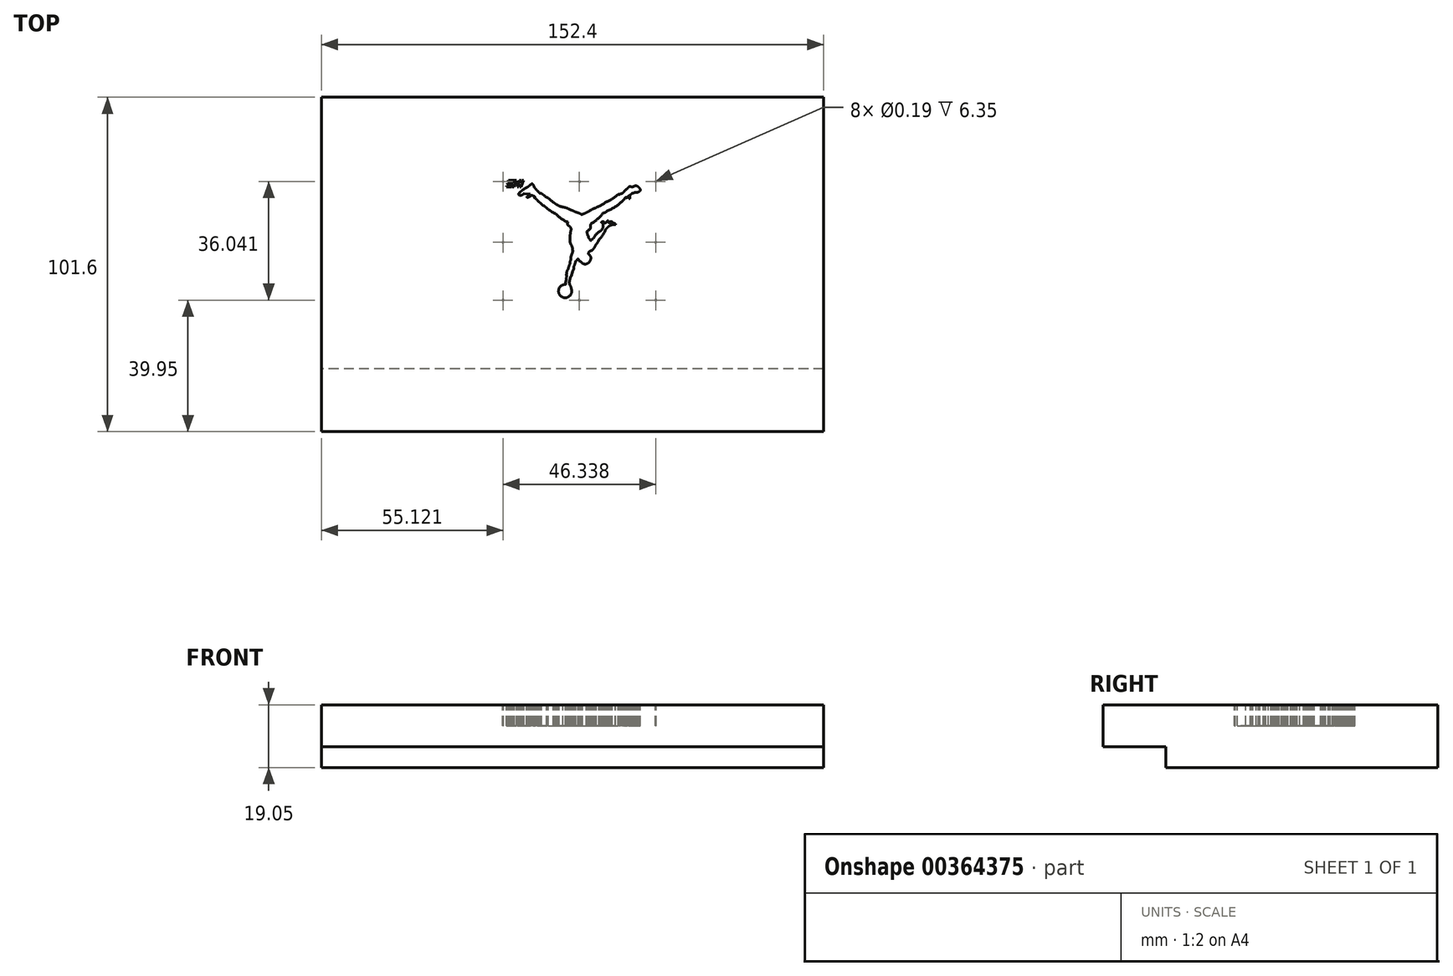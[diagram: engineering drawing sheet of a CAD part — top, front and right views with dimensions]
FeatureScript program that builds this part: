
annotation { "Feature Type Name" : "Feature", "Feature Type Description" : "" }
export const myFeature = defineFeature(function(context is Context, id is Id, definition is map)
    precondition{}
    {
        {
            var Q0;
            Q0=qCreatedBy(makeId("Top.planeOp"),FACE);
            var sketch = newSketch(context, id + "F0", { "sketchPlane" : qUnion([Q0])});
            skLineSegment(sketch, "E0.bottom", {"start": v(-78.3, 43.63) * mm, "end": v(74.1, 43.63) * mm});
            skLineSegment(sketch, "E0.top", {"start": v(-78.3, -57.97) * mm, "end": v(74.1, -57.97) * mm});
            skLineSegment(sketch, "E0.left", {"start": v(-78.3, 43.63) * mm, "end": v(-78.3, -57.97) * mm});
            skLineSegment(sketch, "E0.right", {"start": v(74.1, 43.63) * mm, "end": v(74.1, -57.97) * mm});
            skSolve(sketch);
        }
        {
            var Q0;
            Q0 = qSketchRegion(id + "F0", true);
            extrude(context, id + "F1", {"entities" : qUnion([Q0]), "depth" : 19.05 * mm});
        }
        {
            var Q0;
            Q0=makeQuery(id+"F1.opExtrude","CAP_FACE",FACE,{"disambiguationData":[OSD([sQuery(id+"F0.wireOp",EDGE,"E0.bottom"),sQuery(id+"F0.wireOp",EDGE,"E0.top"),sQuery(id+"F0.wireOp",EDGE,"E0.left"),sQuery(id+"F0.wireOp",EDGE,"E0.right")])],"isStart":true});
            var sketch = newSketch(context, id + "F2", { "sketchPlane" : qUnion([Q0])});
            skLineSegment(sketch, "E1.bottom", {"start": v(74.1, 57.97) * mm, "end": v(-78.3, 57.97) * mm});
            skLineSegment(sketch, "E1.top", {"start": v(74.1, 38.92) * mm, "end": v(-78.3, 38.92) * mm});
            skLineSegment(sketch, "E1.left", {"start": v(74.1, 57.97) * mm, "end": v(74.1, 38.92) * mm});
            skLineSegment(sketch, "E1.right", {"start": v(-78.3, 57.97) * mm, "end": v(-78.3, 38.92) * mm});
            skSolve(sketch);
        }
        {
            var Q0;
            Q0 = qSketchRegion(id + "F2", true);
            extrude(context, id + "F3", {"entities" : qUnion([Q0]), "operationType" : NewBodyOperationType.REMOVE, "oppositeDirection" : true, "depth" : 6.35 * mm});
        }
        {
            var Q0;
            Q0=makeQuery(id+"F1.opExtrude","CAP_FACE",FACE,{"disambiguationData":[OSD([sQuery(id+"F0.wireOp",EDGE,"E0.bottom"),sQuery(id+"F0.wireOp",EDGE,"E0.top"),sQuery(id+"F0.wireOp",EDGE,"E0.left"),sQuery(id+"F0.wireOp",EDGE,"E0.right")])],"isStart":false});
            var sketch = newSketch(context, id + "F4", { "sketchPlane" : qUnion([Q0])});
            skLineSegment(sketch, "E2", {"start": v(-20.56, 18.4) * mm, "end": v(-21.26, 16.34) * mm});
            skLineSegment(sketch, "E3", {"start": v(-21.26, 16.34) * mm, "end": v(-22.15, 16.34) * mm});
            skLineSegment(sketch, "E4", {"start": v(-22.15, 16.34) * mm, "end": v(-22.01, 16.76) * mm});
            skLineSegment(sketch, "E5", {"start": v(-21.49, 18.4) * mm, "end": v(-20.56, 18.4) * mm});
            skLineSegment(sketch, "E6", {"start": v(-18.45, 16.34) * mm, "end": v(-18.9, 16.34) * mm});
            skLineSegment(sketch, "E7", {"start": v(-18.9, 16.34) * mm, "end": v(-18.2, 18.4) * mm});
            skLineSegment(sketch, "E8", {"start": v(-18.2, 18.4) * mm, "end": v(-17.73, 18.4) * mm});
            skLineSegment(sketch, "E9", {"start": v(-17.73, 18.4) * mm, "end": v(-17.77, 17.47) * mm});
            skLineSegment(sketch, "E10", {"start": v(-17.77, 17.47) * mm, "end": v(-17.45, 18.4) * mm});
            skLineSegment(sketch, "E11", {"start": v(-17.45, 18.4) * mm, "end": v(-17, 18.4) * mm});
            skLineSegment(sketch, "E12", {"start": v(-17, 18.4) * mm, "end": v(-17.7, 16.34) * mm});
            skLineSegment(sketch, "E13", {"start": v(-17.7, 16.34) * mm, "end": v(-18.15, 16.34) * mm});
            skLineSegment(sketch, "E14", {"start": v(-18.15, 16.34) * mm, "end": v(-18.14, 17.27) * mm});
            skLineSegment(sketch, "E15", {"start": v(-18.14, 17.27) * mm, "end": v(-18.45, 16.34) * mm});
            skLineSegment(sketch, "E16", {"start": v(-19.11, 16.34) * mm, "end": v(-19.65, 16.34) * mm});
            skLineSegment(sketch, "E17", {"start": v(-19.65, 16.34) * mm, "end": v(-18.95, 18.4) * mm});
            skLineSegment(sketch, "E18", {"start": v(-18.95, 18.4) * mm, "end": v(-18.41, 18.4) * mm});
            skLineSegment(sketch, "E19", {"start": v(-18.41, 18.4) * mm, "end": v(-19.11, 16.34) * mm, "construction": true});
            skLineSegment(sketch, "E20", {"start": v(-20.64, 16.34) * mm, "end": v(-21.14, 16.34) * mm});
            skLineSegment(sketch, "E21", {"start": v(-21.14, 16.34) * mm, "end": v(-20.52, 17.27) * mm});
            skLineSegment(sketch, "E22", {"start": v(-20.52, 17.27) * mm, "end": v(-20.47, 18.4) * mm});
            skLineSegment(sketch, "E23", {"start": v(-20.47, 18.4) * mm, "end": v(-19.92, 18.4) * mm});
            skLineSegment(sketch, "E24", {"start": v(-19.92, 18.4) * mm, "end": v(-20, 17.52) * mm});
            skLineSegment(sketch, "E25", {"start": v(-20, 17.52) * mm, "end": v(-19.7, 18.4) * mm});
            skLineSegment(sketch, "E26", {"start": v(-19.7, 18.4) * mm, "end": v(-19.16, 18.4) * mm});
            skLineSegment(sketch, "E27", {"start": v(-19.16, 18.4) * mm, "end": v(-19.86, 16.34) * mm});
            skLineSegment(sketch, "E28", {"start": v(-19.86, 16.34) * mm, "end": v(-20.4, 16.34) * mm});
            skLineSegment(sketch, "E29", {"start": v(-20.4, 16.34) * mm, "end": v(-20.12, 17.14) * mm});
            skLineSegment(sketch, "E30", {"start": v(-20.12, 17.14) * mm, "end": v(-20.64, 16.34) * mm});
            skCircle(sketch, "E31", {"center": v(23.17, 18.02) * mm, "radius": 0.1 * mm});
            skCircle(sketch, "E32", {"center": v(-23.17, 18.02) * mm, "radius": 0.1 * mm});
            skCircle(sketch, "E33", {"center": v(-23.17, -18.02) * mm, "radius": 0.1 * mm});
            skCircle(sketch, "E34", {"center": v(23.17, -18.02) * mm, "radius": 0.1 * mm});
            skCircle(sketch, "E35", {"center": v(23.17, -0.48) * mm, "radius": 0.1 * mm});
            skCircle(sketch, "E36", {"center": v(0, 18.02) * mm, "radius": 0.1 * mm});
            skCircle(sketch, "E37", {"center": v(-23.17, -0.48) * mm, "radius": 0.1 * mm});
            skCircle(sketch, "E38", {"center": v(0, -18.02) * mm, "radius": 0.1 * mm});
            skLineSegment(sketch, "E39", {"start": v(-3.9, -10.55) * mm, "end": v(-4, -11.58) * mm});
            skLineSegment(sketch, "E40", {"start": v(24.2, 19.05) * mm, "end": v(-24.2, 19.05) * mm, "construction": true});
            skLineSegment(sketch, "E41", {"start": v(-24.2, -19.05) * mm, "end": v(24.2, -19.05) * mm, "construction": true});
            skLineSegment(sketch, "E42", {"start": v(24.2, -19.05) * mm, "end": v(24.2, 19.05) * mm, "construction": true});
            skLineSegment(sketch, "E43", {"start": v(-24.2, 19.05) * mm, "end": v(-24.2, -19.05) * mm, "construction": true});
            skArc(sketch, "E44", {"start": v(-3.94, -10.35) * mm, "mid": v(-3.93, -10.45) * mm, "end": v(-3.9, -10.55) * mm});
            skArc(sketch, "E45", {"start": v(-1.72, -7.9) * mm, "mid": v(-1.37, -7.08) * mm, "end": v(-1.13, -6.21) * mm});
            skArc(sketch, "E46", {"start": v(-1.13, -6.21) * mm, "mid": v(-1.1, -6.16) * mm, "end": v(-1.08, -6.1) * mm});
            skArc(sketch, "E47", {"start": v(-1.75, -8.61) * mm, "mid": v(-1.7, -8.26) * mm, "end": v(-1.72, -7.9) * mm});
            skArc(sketch, "E48", {"start": v(-2.12, -9.3) * mm, "mid": v(-1.92, -8.97) * mm, "end": v(-1.75, -8.61) * mm});
            skArc(sketch, "E49", {"start": v(-2.08, -9.41) * mm, "mid": v(-2.08, -9.35) * mm, "end": v(-2.12, -9.3) * mm});
            skLineSegment(sketch, "E50", {"start": v(-2.49, -10.76) * mm, "end": v(-2.08, -9.41) * mm});
            skArc(sketch, "E51", {"start": v(-2.68, -10.92) * mm, "mid": v(-2.56, -10.87) * mm, "end": v(-2.49, -10.76) * mm});
            skLineSegment(sketch, "E52", {"start": v(-3.12, -12.7) * mm, "end": v(-2.68, -10.92) * mm});
            skArc(sketch, "E53", {"start": v(-2.97, -13.33) * mm, "mid": v(-3.02, -13) * mm, "end": v(-3.12, -12.7) * mm});
            skArc(sketch, "E54", {"start": v(-2.44, -14.7) * mm, "mid": v(-2.62, -13.99) * mm, "end": v(-2.97, -13.33) * mm});
            skArc(sketch, "E55", {"start": v(-4.28, -13.3) * mm, "mid": v(-5.57, -16.9) * mm, "end": v(-2.44, -14.7) * mm});
            skArc(sketch, "E56", {"start": v(-4.28, -13.3) * mm, "mid": v(-4.13, -13.17) * mm, "end": v(-4.19, -12.98) * mm});
            skArc(sketch, "E57", {"start": v(-4.17, -12.53) * mm, "mid": v(-4.23, -12.76) * mm, "end": v(-4.19, -12.98) * mm});
            skArc(sketch, "E58", {"start": v(-4.17, -12.53) * mm, "mid": v(-4.06, -12.06) * mm, "end": v(-4, -11.58) * mm});
            skArc(sketch, "E59", {"start": v(-3.8, -9.3) * mm, "mid": v(-3.9, -9.82) * mm, "end": v(-3.94, -10.35) * mm});
            skArc(sketch, "E60", {"start": v(-3.44, -8.7) * mm, "mid": v(-3.68, -8.97) * mm, "end": v(-3.8, -9.3) * mm});
            skArc(sketch, "E61", {"start": v(-2.87, -6.92) * mm, "mid": v(-3.21, -7.8) * mm, "end": v(-3.44, -8.7) * mm});
            skArc(sketch, "E62", {"start": v(-2.66, -5.86) * mm, "mid": v(-2.83, -6.38) * mm, "end": v(-2.87, -6.92) * mm});
            skArc(sketch, "E63", {"start": v(-2.65, -5.2) * mm, "mid": v(-2.66, -5.53) * mm, "end": v(-2.66, -5.86) * mm});
            skArc(sketch, "E64", {"start": v(-2.47, -4.51) * mm, "mid": v(-2.59, -4.85) * mm, "end": v(-2.65, -5.2) * mm});
            skArc(sketch, "E65", {"start": v(-2.1, -3.69) * mm, "mid": v(-2.3, -4.1) * mm, "end": v(-2.47, -4.51) * mm});
            skArc(sketch, "E66", {"start": v(-2.1, -3.69) * mm, "mid": v(-2.06, -3.55) * mm, "end": v(-2.04, -3.4) * mm});
            skArc(sketch, "E67", {"start": v(-2.04, -3.4) * mm, "mid": v(-2.03, -3.08) * mm, "end": v(-2.04, -2.76) * mm});
            skArc(sketch, "E68", {"start": v(-2.04, -2.76) * mm, "mid": v(-2.11, -2.3) * mm, "end": v(-2.23, -1.83) * mm});
            skArc(sketch, "E69", {"start": v(-2.23, -1.83) * mm, "mid": v(-2.36, -1.49) * mm, "end": v(-2.54, -1.17) * mm});
            skArc(sketch, "E70", {"start": v(-2.8, -0.48) * mm, "mid": v(-2.71, -0.84) * mm, "end": v(-2.54, -1.17) * mm});
            skArc(sketch, "E71", {"start": v(-2.87, 0.87) * mm, "mid": v(-2.85, 0.2) * mm, "end": v(-2.8, -0.48) * mm});
            skArc(sketch, "E72", {"start": v(-2.48, 3.52) * mm, "mid": v(-2.76, 2.21) * mm, "end": v(-2.87, 0.87) * mm});
            skArc(sketch, "E73", {"start": v(-2.77, 4.24) * mm, "mid": v(-2.65, 3.87) * mm, "end": v(-2.48, 3.52) * mm});
            skArc(sketch, "E74", {"start": v(-3.56, 4.85) * mm, "mid": v(-3.2, 4.5) * mm, "end": v(-2.77, 4.24) * mm});
            skArc(sketch, "E75", {"start": v(-3.64, 5.38) * mm, "mid": v(-3.66, 5.1) * mm, "end": v(-3.56, 4.85) * mm});
            skArc(sketch, "E76", {"start": v(-3.5, 5.63) * mm, "mid": v(-3.57, 5.5) * mm, "end": v(-3.64, 5.38) * mm});
            skArc(sketch, "E77", {"start": v(-7.2, 8.26) * mm, "mid": v(-5.5, 6.72) * mm, "end": v(-3.5, 5.63) * mm});
            skArc(sketch, "E78", {"start": v(-7.96, 8.54) * mm, "mid": v(-7.6, 8.35) * mm, "end": v(-7.2, 8.26) * mm});
            skArc(sketch, "E79", {"start": v(-12.78, 12.33) * mm, "mid": v(-10.45, 10.33) * mm, "end": v(-7.96, 8.54) * mm});
            skArc(sketch, "E80", {"start": v(-12.78, 12.33) * mm, "mid": v(-13.08, 12.64) * mm, "end": v(-13.43, 12.89) * mm});
            skArc(sketch, "E81", {"start": v(-13.54, 12.94) * mm, "mid": v(-13.49, 12.91) * mm, "end": v(-13.43, 12.89) * mm});
            skArc(sketch, "E82", {"start": v(-13.6, 13.18) * mm, "mid": v(-13.63, 13.05) * mm, "end": v(-13.54, 12.94) * mm});
            skArc(sketch, "E83", {"start": v(-13.52, 13.33) * mm, "mid": v(-13.56, 13.25) * mm, "end": v(-13.6, 13.18) * mm});
            skArc(sketch, "E84", {"start": v(-13.52, 13.33) * mm, "mid": v(-13.6, 13.47) * mm, "end": v(-13.74, 13.54) * mm});
            skArc(sketch, "E85", {"start": v(-14.02, 13.56) * mm, "mid": v(-13.88, 13.53) * mm, "end": v(-13.74, 13.54) * mm});
            skArc(sketch, "E86", {"start": v(-14.02, 13.56) * mm, "mid": v(-14.15, 13.67) * mm, "end": v(-14.3, 13.78) * mm});
            skArc(sketch, "E87", {"start": v(-14.3, 13.78) * mm, "mid": v(-14.45, 13.82) * mm, "end": v(-14.6, 13.77) * mm});
            skArc(sketch, "E88", {"start": v(-14.6, 13.77) * mm, "mid": v(-14.7, 13.7) * mm, "end": v(-14.78, 13.6) * mm});
            skArc(sketch, "E89", {"start": v(-14.98, 13.6) * mm, "mid": v(-14.88, 13.59) * mm, "end": v(-14.78, 13.6) * mm});
            skArc(sketch, "E90", {"start": v(-15.76, 13.19) * mm, "mid": v(-15.32, 13.3) * mm, "end": v(-14.98, 13.6) * mm});
            skArc(sketch, "E91", {"start": v(-15.9, 13.18) * mm, "mid": v(-15.83, 13.18) * mm, "end": v(-15.76, 13.19) * mm});
            skArc(sketch, "E92", {"start": v(-15.93, 13.35) * mm, "mid": v(-15.98, 13.25) * mm, "end": v(-15.9, 13.18) * mm});
            skArc(sketch, "E93", {"start": v(-15.93, 13.35) * mm, "mid": v(-15.77, 13.39) * mm, "end": v(-15.62, 13.46) * mm});
            skArc(sketch, "E94", {"start": v(-15.62, 13.46) * mm, "mid": v(-15.21, 13.8) * mm, "end": v(-14.9, 14.23) * mm});
            skLineSegment(sketch, "E95", {"start": v(-16.8, 14.28) * mm, "end": v(-14.9, 14.23) * mm});
            skArc(sketch, "E96", {"start": v(-16.8, 14.28) * mm, "mid": v(-16.96, 14.22) * mm, "end": v(-17.1, 14.13) * mm});
            skArc(sketch, "E97", {"start": v(-17.67, 13.8) * mm, "mid": v(-17.37, 13.94) * mm, "end": v(-17.1, 14.13) * mm});
            skArc(sketch, "E98", {"start": v(-18.09, 13.8) * mm, "mid": v(-17.88, 13.77) * mm, "end": v(-17.67, 13.8) * mm});
            skArc(sketch, "E99", {"start": v(-18.46, 14.04) * mm, "mid": v(-18.3, 13.88) * mm, "end": v(-18.09, 13.8) * mm});
            skArc(sketch, "E100", {"start": v(-18.48, 14.26) * mm, "mid": v(-18.5, 14.15) * mm, "end": v(-18.46, 14.04) * mm});
            skArc(sketch, "E101", {"start": v(-17.16, 15.47) * mm, "mid": v(-17.84, 14.9) * mm, "end": v(-18.48, 14.26) * mm});
            skArc(sketch, "E102", {"start": v(-16.05, 16.16) * mm, "mid": v(-16.63, 15.85) * mm, "end": v(-17.16, 15.47) * mm});
            skArc(sketch, "E103", {"start": v(-16.05, 16.16) * mm, "mid": v(-15.58, 16.42) * mm, "end": v(-15.16, 16.75) * mm});
            skArc(sketch, "E104", {"start": v(-14.47, 17.28) * mm, "mid": v(-14.84, 17.05) * mm, "end": v(-15.16, 16.75) * mm});
            skArc(sketch, "E105", {"start": v(-14.19, 17.24) * mm, "mid": v(-14.32, 17.3) * mm, "end": v(-14.47, 17.28) * mm});
            skArc(sketch, "E106", {"start": v(-13.74, 16.38) * mm, "mid": v(-13.93, 16.83) * mm, "end": v(-14.19, 17.24) * mm});
            skArc(sketch, "E107", {"start": v(-13.72, 16.24) * mm, "mid": v(-13.73, 16.31) * mm, "end": v(-13.74, 16.38) * mm});
            skArc(sketch, "E108", {"start": v(-13.05, 15.43) * mm, "mid": v(-13.34, 15.87) * mm, "end": v(-13.72, 16.24) * mm});
            skArc(sketch, "E109", {"start": v(-12.41, 14.78) * mm, "mid": v(-12.7, 15.14) * mm, "end": v(-13.05, 15.43) * mm});
            skArc(sketch, "E110", {"start": v(-12.41, 14.78) * mm, "mid": v(-12.23, 14.6) * mm, "end": v(-12.03, 14.44) * mm});
            skArc(sketch, "E111", {"start": v(-11.5, 14.35) * mm, "mid": v(-11.76, 14.43) * mm, "end": v(-12.03, 14.44) * mm});
            skArc(sketch, "E112", {"start": v(-10.03, 13.2) * mm, "mid": v(-10.75, 13.8) * mm, "end": v(-11.5, 14.35) * mm});
            skArc(sketch, "E113", {"start": v(-9.42, 12.95) * mm, "mid": v(-9.71, 13.1) * mm, "end": v(-10.03, 13.2) * mm});
            skArc(sketch, "E114", {"start": v(-9.42, 12.95) * mm, "mid": v(-8.57, 12.2) * mm, "end": v(-7.66, 11.52) * mm});
            skArc(sketch, "E115", {"start": v(-7.66, 11.52) * mm, "mid": v(-7.3, 11.23) * mm, "end": v(-6.91, 10.98) * mm});
            skArc(sketch, "E116", {"start": v(-6.18, 10.54) * mm, "mid": v(-6.53, 10.79) * mm, "end": v(-6.91, 10.98) * mm});
            skArc(sketch, "E117", {"start": v(-6.18, 10.54) * mm, "mid": v(-5.6, 10.38) * mm, "end": v(-5.02, 10.25) * mm});
            skArc(sketch, "E118", {"start": v(-3.08, 9.6) * mm, "mid": v(-4.03, 10) * mm, "end": v(-5.02, 10.25) * mm});
            skArc(sketch, "E119", {"start": v(-3.08, 9.6) * mm, "mid": v(-2.81, 9.45) * mm, "end": v(-2.52, 9.33) * mm});
            skArc(sketch, "E120", {"start": v(-1.2, 8.76) * mm, "mid": v(-1.86, 9.06) * mm, "end": v(-2.52, 9.33) * mm});
            skArc(sketch, "E121", {"start": v(0.56, 8.04) * mm, "mid": v(-0.3, 8.45) * mm, "end": v(-1.2, 8.76) * mm});
            skArc(sketch, "E122", {"start": v(0.56, 8.04) * mm, "mid": v(0.77, 8) * mm, "end": v(0.98, 8.06) * mm});
            skArc(sketch, "E123", {"start": v(0.98, 8.06) * mm, "mid": v(1.95, 8.49) * mm, "end": v(2.89, 9) * mm});
            skArc(sketch, "E124", {"start": v(6.07, 10.48) * mm, "mid": v(4.44, 9.8) * mm, "end": v(2.89, 9) * mm});
            skArc(sketch, "E125", {"start": v(9.63, 12.55) * mm, "mid": v(7.81, 11.58) * mm, "end": v(6.07, 10.48) * mm});
            skArc(sketch, "E126", {"start": v(9.63, 12.55) * mm, "mid": v(10.73, 13.26) * mm, "end": v(11.76, 14.08) * mm});
            skArc(sketch, "E127", {"start": v(11.97, 14.1) * mm, "mid": v(11.86, 14.12) * mm, "end": v(11.76, 14.08) * mm});
            skArc(sketch, "E128", {"start": v(12.08, 14.05) * mm, "mid": v(12.03, 14.08) * mm, "end": v(11.97, 14.1) * mm});
            skArc(sketch, "E129", {"start": v(12.08, 14.05) * mm, "mid": v(12.15, 14.03) * mm, "end": v(12.2, 14.06) * mm});
            skArc(sketch, "E130", {"start": v(12.59, 14.33) * mm, "mid": v(12.4, 14.2) * mm, "end": v(12.2, 14.06) * mm});
            skArc(sketch, "E131", {"start": v(12.84, 14.36) * mm, "mid": v(12.71, 14.36) * mm, "end": v(12.59, 14.33) * mm});
            skArc(sketch, "E132", {"start": v(13.09, 14.49) * mm, "mid": v(12.96, 14.44) * mm, "end": v(12.84, 14.36) * mm});
            skArc(sketch, "E133", {"start": v(13.09, 14.49) * mm, "mid": v(13.23, 14.61) * mm, "end": v(13.33, 14.78) * mm});
            skArc(sketch, "E134", {"start": v(13.48, 14.83) * mm, "mid": v(13.4, 14.82) * mm, "end": v(13.33, 14.78) * mm});
            skArc(sketch, "E135", {"start": v(13.48, 14.83) * mm, "mid": v(13.66, 15.03) * mm, "end": v(13.79, 15.25) * mm});
            skArc(sketch, "E136", {"start": v(14.1, 15.53) * mm, "mid": v(13.92, 15.43) * mm, "end": v(13.79, 15.25) * mm});
            skArc(sketch, "E137", {"start": v(14.27, 15.55) * mm, "mid": v(14.19, 15.55) * mm, "end": v(14.1, 15.53) * mm});
            skArc(sketch, "E138", {"start": v(14.27, 15.55) * mm, "mid": v(14.4, 15.68) * mm, "end": v(14.49, 15.83) * mm});
            skArc(sketch, "E139", {"start": v(14.65, 15.96) * mm, "mid": v(14.54, 15.93) * mm, "end": v(14.49, 15.83) * mm});
            skArc(sketch, "E140", {"start": v(14.76, 16.17) * mm, "mid": v(14.69, 16.07) * mm, "end": v(14.65, 15.96) * mm});
            skArc(sketch, "E141", {"start": v(15.05, 16.41) * mm, "mid": v(14.9, 16.3) * mm, "end": v(14.76, 16.17) * mm});
            skArc(sketch, "E142", {"start": v(15.34, 16.47) * mm, "mid": v(15.2, 16.46) * mm, "end": v(15.05, 16.41) * mm});
            skArc(sketch, "E143", {"start": v(15.55, 16.47) * mm, "mid": v(15.44, 16.47) * mm, "end": v(15.34, 16.47) * mm});
            skArc(sketch, "E144", {"start": v(15.55, 16.47) * mm, "mid": v(16, 16.37) * mm, "end": v(16.45, 16.48) * mm});
            skArc(sketch, "E145", {"start": v(16.45, 16.48) * mm, "mid": v(16.61, 16.57) * mm, "end": v(16.76, 16.67) * mm});
            skArc(sketch, "E146", {"start": v(17.45, 16.64) * mm, "mid": v(17.1, 16.7) * mm, "end": v(16.76, 16.67) * mm});
            skArc(sketch, "E147", {"start": v(18.02, 16.22) * mm, "mid": v(17.76, 16.46) * mm, "end": v(17.45, 16.64) * mm});
            skArc(sketch, "E148", {"start": v(18.47, 15.58) * mm, "mid": v(18.27, 15.92) * mm, "end": v(18.02, 16.22) * mm});
            skArc(sketch, "E149", {"start": v(18.46, 15.27) * mm, "mid": v(18.5, 15.42) * mm, "end": v(18.47, 15.58) * mm});
            skArc(sketch, "E150", {"start": v(17.94, 14.81) * mm, "mid": v(18.22, 15.01) * mm, "end": v(18.46, 15.27) * mm});
            skArc(sketch, "E151", {"start": v(17.24, 14.7) * mm, "mid": v(17.6, 14.72) * mm, "end": v(17.94, 14.81) * mm});
            skLineSegment(sketch, "E152", {"start": v(16.95, 14.7) * mm, "end": v(17.24, 14.7) * mm});
            skArc(sketch, "E153", {"start": v(16.95, 14.7) * mm, "mid": v(16.6, 14.6) * mm, "end": v(16.26, 14.44) * mm});
            skLineSegment(sketch, "E154", {"start": v(16.05, 14.44) * mm, "end": v(16.26, 14.44) * mm});
            skArc(sketch, "E155", {"start": v(15.65, 14.26) * mm, "mid": v(15.86, 14.34) * mm, "end": v(16.05, 14.44) * mm});
            skArc(sketch, "E156", {"start": v(15.64, 14.04) * mm, "mid": v(15.66, 14.15) * mm, "end": v(15.65, 14.26) * mm});
            skArc(sketch, "E157", {"start": v(15.42, 13.84) * mm, "mid": v(15.55, 13.92) * mm, "end": v(15.64, 14.04) * mm});
            skArc(sketch, "E158", {"start": v(15.24, 13.86) * mm, "mid": v(15.32, 13.83) * mm, "end": v(15.42, 13.84) * mm});
            skArc(sketch, "E159", {"start": v(15.24, 13.86) * mm, "mid": v(15.15, 13.85) * mm, "end": v(15.16, 13.77) * mm});
            skArc(sketch, "E160", {"start": v(15.25, 13.42) * mm, "mid": v(15.23, 13.6) * mm, "end": v(15.16, 13.77) * mm});
            skArc(sketch, "E161", {"start": v(15.25, 13.42) * mm, "mid": v(15.26, 13.3) * mm, "end": v(15.29, 13.2) * mm});
            skArc(sketch, "E162", {"start": v(15.32, 12.9) * mm, "mid": v(15.33, 13.05) * mm, "end": v(15.29, 13.2) * mm});
            skArc(sketch, "E163", {"start": v(15.2, 12.77) * mm, "mid": v(15.28, 12.82) * mm, "end": v(15.32, 12.9) * mm});
            skArc(sketch, "E164", {"start": v(15.05, 12.88) * mm, "mid": v(15.1, 12.8) * mm, "end": v(15.2, 12.77) * mm});
            skArc(sketch, "E165", {"start": v(14.95, 13.3) * mm, "mid": v(14.98, 13.09) * mm, "end": v(15.05, 12.88) * mm});
            skArc(sketch, "E166", {"start": v(14.95, 13.3) * mm, "mid": v(14.94, 13.4) * mm, "end": v(14.88, 13.48) * mm});
            skArc(sketch, "E167", {"start": v(14.88, 13.48) * mm, "mid": v(14.78, 13.5) * mm, "end": v(14.68, 13.47) * mm});
            skArc(sketch, "E168", {"start": v(14.68, 13.47) * mm, "mid": v(14.62, 13.38) * mm, "end": v(14.58, 13.28) * mm});
            skArc(sketch, "E169", {"start": v(14.4, 13.06) * mm, "mid": v(14.52, 13.15) * mm, "end": v(14.58, 13.28) * mm});
            skArc(sketch, "E170", {"start": v(14.18, 13.09) * mm, "mid": v(14.29, 13.05) * mm, "end": v(14.4, 13.06) * mm});
            skArc(sketch, "E171", {"start": v(14.04, 13.21) * mm, "mid": v(14.1, 13.14) * mm, "end": v(14.18, 13.09) * mm});
            skArc(sketch, "E172", {"start": v(13.8, 13.05) * mm, "mid": v(13.93, 13.1) * mm, "end": v(14.04, 13.21) * mm});
            skArc(sketch, "E173", {"start": v(13.8, 13.05) * mm, "mid": v(13.78, 13) * mm, "end": v(13.83, 12.96) * mm});
            skArc(sketch, "E174", {"start": v(13.83, 12.78) * mm, "mid": v(13.88, 12.87) * mm, "end": v(13.83, 12.96) * mm});
            skArc(sketch, "E175", {"start": v(13.83, 12.78) * mm, "mid": v(13.4, 12.45) * mm, "end": v(13.04, 12.06) * mm});
            skArc(sketch, "E176", {"start": v(8.45, 9.11) * mm, "mid": v(10.9, 10.33) * mm, "end": v(13.04, 12.06) * mm});
            skArc(sketch, "E177", {"start": v(7.2, 8.47) * mm, "mid": v(7.9, 8.64) * mm, "end": v(8.45, 9.11) * mm});
            skArc(sketch, "E178", {"start": v(4.65, 5.97) * mm, "mid": v(6.05, 7.1) * mm, "end": v(7.2, 8.47) * mm});
            skArc(sketch, "E179", {"start": v(3.95, 5.48) * mm, "mid": v(4.37, 5.63) * mm, "end": v(4.65, 5.97) * mm});
            skArc(sketch, "E180", {"start": v(3.95, 5.48) * mm, "mid": v(3.75, 5.4) * mm, "end": v(3.58, 5.25) * mm});
            skArc(sketch, "E181", {"start": v(3.58, 5.25) * mm, "mid": v(3.42, 4.91) * mm, "end": v(3.38, 4.54) * mm});
            skArc(sketch, "E182", {"start": v(3.37, 3.98) * mm, "mid": v(3.4, 4.26) * mm, "end": v(3.38, 4.54) * mm});
            skArc(sketch, "E183", {"start": v(3.12, 3.42) * mm, "mid": v(3.28, 3.68) * mm, "end": v(3.37, 3.98) * mm});
            skArc(sketch, "E184", {"start": v(2.63, 3.25) * mm, "mid": v(2.9, 3.27) * mm, "end": v(3.12, 3.42) * mm});
            skArc(sketch, "E185", {"start": v(2.25, 2.76) * mm, "mid": v(2.45, 3) * mm, "end": v(2.63, 3.25) * mm});
            skArc(sketch, "E186", {"start": v(2.47, 1.7) * mm, "mid": v(2.38, 2.23) * mm, "end": v(2.25, 2.76) * mm});
            skArc(sketch, "E187", {"start": v(2.75, 0.97) * mm, "mid": v(2.73, 1.38) * mm, "end": v(2.47, 1.7) * mm});
            skArc(sketch, "E188", {"start": v(3.31, 0.14) * mm, "mid": v(3.06, 0.58) * mm, "end": v(2.75, 0.97) * mm});
            skArc(sketch, "E189", {"start": v(3.31, 0.14) * mm, "mid": v(3.46, 0.1) * mm, "end": v(3.6, 0.1) * mm});
            skArc(sketch, "E190", {"start": v(4.2, 0.59) * mm, "mid": v(3.81, 0.46) * mm, "end": v(3.6, 0.1) * mm});
            skArc(sketch, "E191", {"start": v(6.35, 2.93) * mm, "mid": v(5.07, 1.94) * mm, "end": v(4.2, 0.59) * mm});
            skArc(sketch, "E192", {"start": v(6.35, 2.93) * mm, "mid": v(7, 3.67) * mm, "end": v(7.23, 4.62) * mm});
            skArc(sketch, "E193", {"start": v(7.23, 4.62) * mm, "mid": v(7.22, 4.72) * mm, "end": v(7.2, 4.82) * mm});
            skArc(sketch, "E194", {"start": v(7.23, 5.07) * mm, "mid": v(7.2, 4.95) * mm, "end": v(7.2, 4.82) * mm});
            skArc(sketch, "E195", {"start": v(7.23, 5.07) * mm, "mid": v(7.24, 5.15) * mm, "end": v(7.22, 5.22) * mm});
            skArc(sketch, "E196", {"start": v(7.22, 5.22) * mm, "mid": v(7.12, 5.33) * mm, "end": v(6.99, 5.4) * mm});
            skArc(sketch, "E197", {"start": v(6.74, 5.5) * mm, "mid": v(6.86, 5.43) * mm, "end": v(6.99, 5.4) * mm});
            skArc(sketch, "E198", {"start": v(6.78, 5.77) * mm, "mid": v(6.71, 5.64) * mm, "end": v(6.74, 5.5) * mm});
            skArc(sketch, "E199", {"start": v(7.3, 5.78) * mm, "mid": v(7.04, 5.84) * mm, "end": v(6.78, 5.77) * mm});
            skArc(sketch, "E200", {"start": v(7.76, 5.42) * mm, "mid": v(7.56, 5.63) * mm, "end": v(7.3, 5.78) * mm});
            skArc(sketch, "E201", {"start": v(7.76, 5.42) * mm, "mid": v(7.85, 5.4) * mm, "end": v(7.93, 5.43) * mm});
            skLineSegment(sketch, "E202", {"start": v(8.3, 5.86) * mm, "end": v(7.93, 5.43) * mm});
            skArc(sketch, "E203", {"start": v(8.54, 6.04) * mm, "mid": v(8.41, 5.96) * mm, "end": v(8.3, 5.86) * mm});
            skArc(sketch, "E204", {"start": v(8.74, 6.08) * mm, "mid": v(8.63, 6.07) * mm, "end": v(8.54, 6.04) * mm});
            skArc(sketch, "E205", {"start": v(8.84, 5.88) * mm, "mid": v(8.84, 6) * mm, "end": v(8.74, 6.08) * mm});
            skArc(sketch, "E206", {"start": v(8.69, 5.63) * mm, "mid": v(8.77, 5.75) * mm, "end": v(8.84, 5.88) * mm});
            skArc(sketch, "E207", {"start": v(8.69, 5.63) * mm, "mid": v(8.69, 5.57) * mm, "end": v(8.74, 5.55) * mm});
            skArc(sketch, "E208", {"start": v(8.74, 5.55) * mm, "mid": v(8.93, 5.6) * mm, "end": v(9.12, 5.67) * mm});
            skArc(sketch, "E209", {"start": v(9.55, 5.81) * mm, "mid": v(9.32, 5.76) * mm, "end": v(9.12, 5.67) * mm});
            skArc(sketch, "E210", {"start": v(9.9, 5.79) * mm, "mid": v(9.73, 5.82) * mm, "end": v(9.55, 5.81) * mm});
            skArc(sketch, "E211", {"start": v(9.99, 5.64) * mm, "mid": v(9.99, 5.73) * mm, "end": v(9.9, 5.79) * mm});
            skArc(sketch, "E212", {"start": v(9.74, 5.48) * mm, "mid": v(9.88, 5.54) * mm, "end": v(9.99, 5.64) * mm});
            skArc(sketch, "E213", {"start": v(9.74, 5.48) * mm, "mid": v(9.53, 5.4) * mm, "end": v(9.33, 5.28) * mm});
            skArc(sketch, "E214", {"start": v(9.33, 5.28) * mm, "mid": v(9.33, 5.23) * mm, "end": v(9.38, 5.21) * mm});
            skArc(sketch, "E215", {"start": v(10.84, 5.22) * mm, "mid": v(10.11, 5.28) * mm, "end": v(9.38, 5.21) * mm});
            skArc(sketch, "E216", {"start": v(10.97, 5.09) * mm, "mid": v(10.94, 5.18) * mm, "end": v(10.84, 5.22) * mm});
            skArc(sketch, "E217", {"start": v(10.91, 4.96) * mm, "mid": v(10.96, 5.02) * mm, "end": v(10.97, 5.09) * mm});
            skArc(sketch, "E218", {"start": v(10.91, 4.96) * mm, "mid": v(10.3, 4.91) * mm, "end": v(9.7, 4.82) * mm});
            skArc(sketch, "E219", {"start": v(9.7, 4.82) * mm, "mid": v(9.27, 4.64) * mm, "end": v(8.88, 4.4) * mm});
            skArc(sketch, "E220", {"start": v(8.67, 4.15) * mm, "mid": v(8.78, 4.27) * mm, "end": v(8.88, 4.4) * mm});
            skArc(sketch, "E221", {"start": v(8.67, 4.15) * mm, "mid": v(8.29, 3.8) * mm, "end": v(7.96, 3.4) * mm});
            skArc(sketch, "E222", {"start": v(5.86, 0.24) * mm, "mid": v(7.06, 1.72) * mm, "end": v(7.96, 3.4) * mm});
            skArc(sketch, "E223", {"start": v(5.1, -1.02) * mm, "mid": v(5.56, -0.44) * mm, "end": v(5.86, 0.24) * mm});
            skArc(sketch, "E224", {"start": v(4.25, -2.45) * mm, "mid": v(4.72, -1.76) * mm, "end": v(5.1, -1.02) * mm});
            skArc(sketch, "E225", {"start": v(3.84, -2.9) * mm, "mid": v(4.07, -2.7) * mm, "end": v(4.25, -2.45) * mm});
            skArc(sketch, "E226", {"start": v(3.35, -3.04) * mm, "mid": v(3.61, -3.01) * mm, "end": v(3.84, -2.9) * mm});
            skArc(sketch, "E227", {"start": v(3.35, -3.04) * mm, "mid": v(3.04, -3.26) * mm, "end": v(2.82, -3.57) * mm});
            skArc(sketch, "E228", {"start": v(2.66, -3.95) * mm, "mid": v(2.76, -3.77) * mm, "end": v(2.82, -3.57) * mm});
            skArc(sketch, "E229", {"start": v(3.43, -4.97) * mm, "mid": v(3.14, -4.4) * mm, "end": v(2.66, -3.95) * mm});
            skArc(sketch, "E230", {"start": v(3.37, -5.82) * mm, "mid": v(3.46, -5.4) * mm, "end": v(3.43, -4.97) * mm});
            skArc(sketch, "E231", {"start": v(2.06, -7.06) * mm, "mid": v(2.86, -6.59) * mm, "end": v(3.37, -5.82) * mm});
            skArc(sketch, "E232", {"start": v(0.9, -6.84) * mm, "mid": v(1.46, -7.07) * mm, "end": v(2.06, -7.06) * mm});
            skArc(sketch, "E233", {"start": v(0.9, -6.84) * mm, "mid": v(0.7, -6.62) * mm, "end": v(0.49, -6.42) * mm});
            skArc(sketch, "E234", {"start": v(0.27, -6.23) * mm, "mid": v(0.35, -6.35) * mm, "end": v(0.49, -6.42) * mm});
            skArc(sketch, "E235", {"start": v(-0.1, -6.12) * mm, "mid": v(0.08, -6.19) * mm, "end": v(0.27, -6.23) * mm});
            skArc(sketch, "E236", {"start": v(-0.22, -6) * mm, "mid": v(-0.17, -6.08) * mm, "end": v(-0.1, -6.12) * mm});
            skArc(sketch, "E237", {"start": v(-0.2, -5.73) * mm, "mid": v(-0.23, -5.87) * mm, "end": v(-0.22, -6) * mm});
            skArc(sketch, "E238", {"start": v(-0.42, -5.38) * mm, "mid": v(-0.35, -5.58) * mm, "end": v(-0.2, -5.73) * mm});
            skArc(sketch, "E239", {"start": v(-1.08, -6.1) * mm, "mid": v(-0.7, -5.8) * mm, "end": v(-0.42, -5.38) * mm});
            skLineSegment(sketch, "E240", {"start": v(-22.01, 16.76) * mm, "end": v(-21.65, 16.76) * mm});
            skLineSegment(sketch, "E241", {"start": v(-21.52, 17.15) * mm, "end": v(-21.86, 17.15) * mm});
            skLineSegment(sketch, "E242", {"start": v(-21.86, 17.15) * mm, "end": v(-21.72, 17.54) * mm});
            skLineSegment(sketch, "E243", {"start": v(-21.65, 16.76) * mm, "end": v(-21.52, 17.15) * mm});
            skLineSegment(sketch, "E244", {"start": v(-21.72, 17.54) * mm, "end": v(-21.39, 17.54) * mm});
            skLineSegment(sketch, "E245", {"start": v(-21.39, 17.54) * mm, "end": v(-21.23, 18) * mm});
            skLineSegment(sketch, "E246", {"start": v(-21.23, 18) * mm, "end": v(-21.63, 18) * mm});
            skLineSegment(sketch, "E247", {"start": v(-21.63, 18) * mm, "end": v(-21.49, 18.4) * mm});
            skSolve(sketch);
        }
        {
            var Q0;
            Q0 = qSketchRegion(id + "F4", true);
            extrude(context, id + "F5", {"entities" : qUnion([Q0]), "operationType" : NewBodyOperationType.REMOVE, "oppositeDirection" : true, "depth" : 6.35 * mm});
        }
    });
